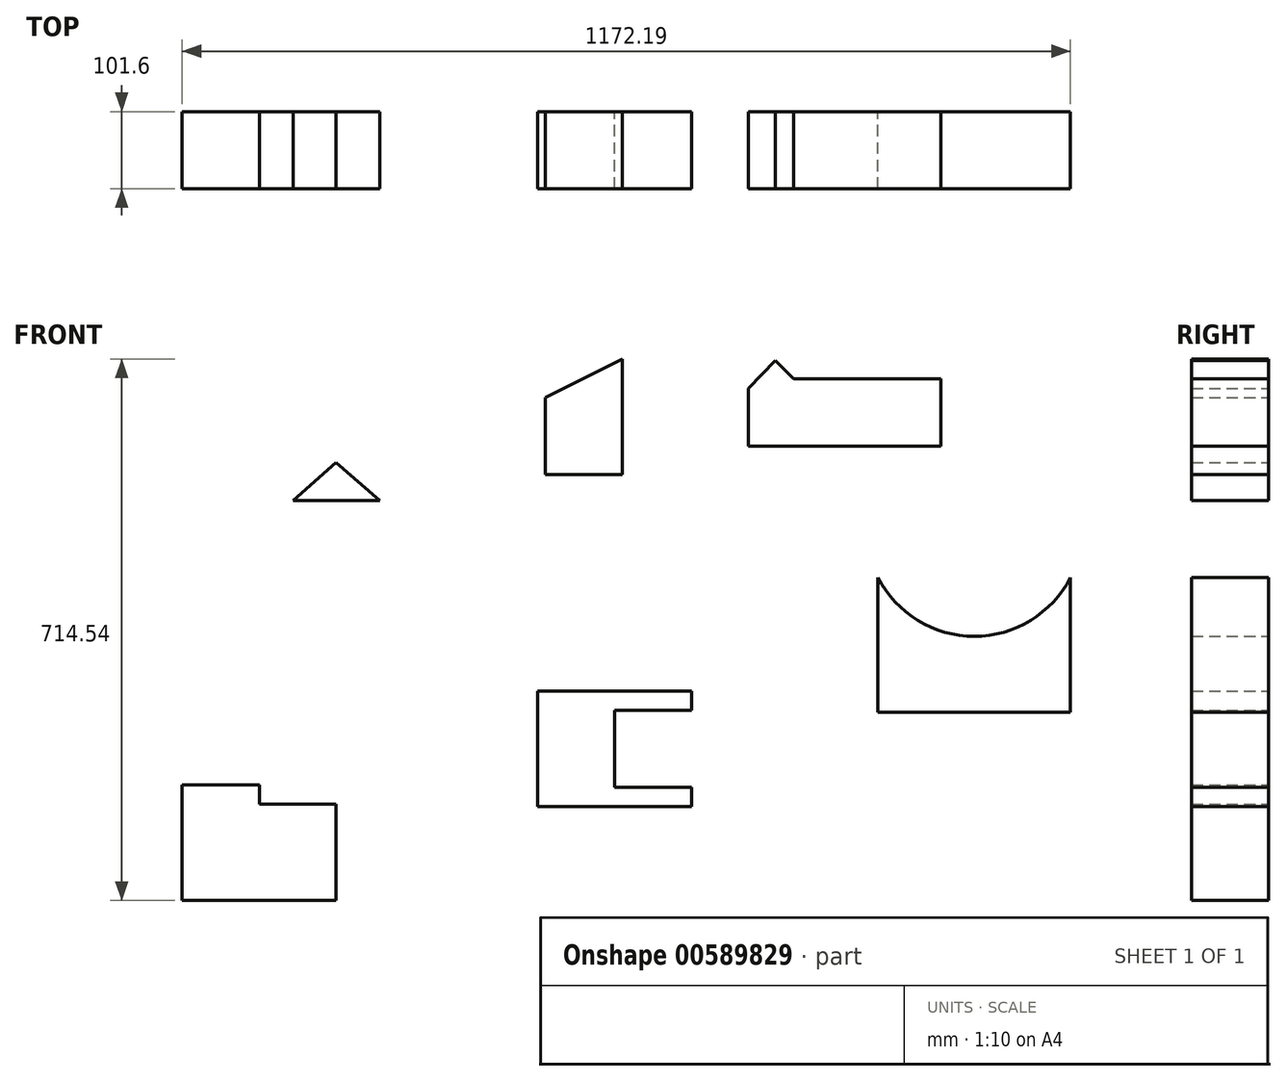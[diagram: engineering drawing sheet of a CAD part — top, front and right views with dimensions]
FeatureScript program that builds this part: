
annotation { "Feature Type Name" : "Feature", "Feature Type Description" : "" }
export const myFeature = defineFeature(function(context is Context, id is Id, definition is map)
    precondition{}
    {
        {
            var Q0;
            Q0=qCreatedBy(makeId("Front.planeOp"),FACE);
            var sketch = newSketch(context, id + "F0", { "sketchPlane" : qUnion([Q0])});
            skLineSegment(sketch, "E0", {"start": v(0, 0) * mm, "end": v(-114.3, -100.8) * mm});
            skLineSegment(sketch, "E1", {"start": v(-114.3, -100.8) * mm, "end": v(114.3, -100.8) * mm});
            skLineSegment(sketch, "E2", {"start": v(0, 0) * mm, "end": v(114.3, -100.8) * mm});
            skLineSegment(sketch, "E3", {"start": v(-57.15, -50.4) * mm, "end": v(57.15, -50.4) * mm});
            skSolve(sketch);
        }
        {
            var Q0;
            {var subQ0=sQuery(id+"F0.wireOp",EDGE,"E1");Q0=makeQuery(id+"F0.imprint","IMPRINT",FACE,{"disambiguationData":[TD([[makeQuery(id+"F0.imprint","IMPRINT",EDGE,{"derivedFrom":subQ0}),1.0]])]});}
            var sketch = newSketch(context, id + "F1", { "sketchPlane" : qUnion([Q0])});
            skSolve(sketch);
        }
        {
            var Q0;
            {var subQ3=sQuery(id+"F0.wireOp",EDGE,"E3");Q0=makeQuery(id+"F0.imprint","IMPRINT",FACE,{"disambiguationData":[TD([[makeQuery(id+"F0.imprint","IMPRINT",EDGE,{"derivedFrom":subQ3}),1.0]])]});}
            var Q1;
            {var subQ0=sQuery(id+"F0.wireOp",EDGE,"E1");Q1=makeQuery(id+"F1.imprint","IMPRINT",FACE,{"disambiguationData":[TD([[makeQuery(id+"F1.imprint","IMPRINT",EDGE,{"derivedFrom":makeQuery(id+"F0.imprint","IMPRINT",EDGE,{"derivedFrom":subQ0})}),1.0]])]});}
            extrude(context, id + "F2", {"entities" : qUnion([Q0, Q1]), "depth" : 101.6 * mm, "offsetDistance" : 25.4 * mm});
        }
        {
            var Q0;
            Q0=qCreatedBy(makeId("Front.planeOp"),FACE);
            var sketch = newSketch(context, id + "F3", { "sketchPlane" : qUnion([Q0])});
            skLineSegment(sketch, "E4", {"start": v(377.76, 136.53) * mm, "end": v(377.76, -15.87) * mm});
            skLineSegment(sketch, "E5", {"start": v(377.76, -15.87) * mm, "end": v(276.16, -15.87) * mm});
            skLineSegment(sketch, "E6", {"start": v(276.16, -15.87) * mm, "end": v(276.16, 85.73) * mm});
            skLineSegment(sketch, "E7", {"start": v(276.16, 85.73) * mm, "end": v(377.76, 136.53) * mm});
            skLineSegment(sketch, "E8", {"start": v(543.89, 21.92) * mm, "end": v(543.89, 98.12) * mm});
            skLineSegment(sketch, "E9", {"start": v(543.89, 21.92) * mm, "end": v(645.49, 21.92) * mm});
            skLineSegment(sketch, "E10", {"start": v(645.49, 21.92) * mm, "end": v(797.89, 21.92) * mm});
            skPoint(sketch, "E10.endSnap0", {"position": v(594.69, 21.92) * mm});
            skLineSegment(sketch, "E11", {"start": v(797.89, 21.92) * mm, "end": v(797.89, 72.72) * mm});
            skLineSegment(sketch, "E12", {"start": v(797.89, 72.72) * mm, "end": v(797.89, 110.82) * mm});
            skLineSegment(sketch, "E13", {"start": v(543.89, 98.12) * mm, "end": v(579.44, 134.4) * mm});
            skLineSegment(sketch, "E14", {"start": v(797.89, 110.82) * mm, "end": v(603.52, 110.82) * mm});
            skLineSegment(sketch, "E15", {"start": v(594.69, 21.92) * mm, "end": v(594.69, 72.72) * mm});
            skLineSegment(sketch, "E16", {"start": v(594.69, 72.72) * mm, "end": v(594.69, 119.47) * mm});
            skLineSegment(sketch, "E17", {"start": v(594.69, 72.72) * mm, "end": v(797.89, 72.72) * mm});
            skLineSegment(sketch, "E18", {"start": v(579.44, 134.4) * mm, "end": v(642.41, 72.72) * mm});
            skSolve(sketch);
        }
        {
            var Q0;
            Q0=makeQuery(id+"F3.imprint","IMPRINT",FACE,{"disambiguationData":[TD([[makeQuery(id+"F3.imprint","IMPRINT",EDGE,{"derivedFrom":sQuery(id+"F3.wireOp",EDGE,"E4")}),-1.0]])]});
            var Q1;
            {var subQ3=sQuery(id+"F3.wireOp",EDGE,"E8");Q1=makeQuery(id+"F3.imprint","IMPRINT",FACE,{"disambiguationData":[TD([[makeQuery(id+"F3.imprint","IMPRINT",EDGE,{"derivedFrom":subQ3}),-1.0]])]});}
            var Q2;
            {var subQ0=sQuery(id+"F3.wireOp",EDGE,"E12");Q2=makeQuery(id+"F3.imprint","IMPRINT",FACE,{"disambiguationData":[TD([[makeQuery(id+"F3.imprint","IMPRINT",EDGE,{"derivedFrom":subQ0}),1.0]])]});}
            var Q3;
            {var subQ2=sQuery(id+"F3.wireOp",EDGE,"E10");Q3=makeQuery(id+"F3.imprint","IMPRINT",FACE,{"disambiguationData":[TD([[makeQuery(id+"F3.imprint","IMPRINT",EDGE,{"derivedFrom":subQ2}),1.0]])]});}
            var Q4;
            {var subQ0=sQuery(id+"F3.wireOp",EDGE,"E16");Q4=makeQuery(id+"F3.imprint","IMPRINT",FACE,{"disambiguationData":[TD([[makeQuery(id+"F3.imprint","IMPRINT",EDGE,{"derivedFrom":subQ0}),-1.0]])]});}
            extrude(context, id + "F4", {"entities" : qUnion([Q0, Q1, Q2, Q3, Q4]), "depth" : 101.6 * mm, "offsetDistance" : 25.4 * mm});
        }
        {
            var Q0;
            Q0=qCreatedBy(makeId("Front.planeOp"),FACE);
            var sketch = newSketch(context, id + "F5", { "sketchPlane" : qUnion([Q0])});
            skLineSegment(sketch, "E19", {"start": v(-203.2, -425.61) * mm, "end": v(-101.6, -425.61) * mm});
            skLineSegment(sketch, "E20", {"start": v(-101.6, -425.61) * mm, "end": v(-101.6, -451.01) * mm});
            skLineSegment(sketch, "E21", {"start": v(-101.6, -451.01) * mm, "end": v(0, -451.01) * mm});
            skLineSegment(sketch, "E22", {"start": v(0, -451.01) * mm, "end": v(0, -578.01) * mm});
            skLineSegment(sketch, "E23", {"start": v(0, -578.01) * mm, "end": v(-203.2, -578.01) * mm});
            skLineSegment(sketch, "E24", {"start": v(-203.2, -578.01) * mm, "end": v(-203.2, -425.61) * mm});
            skSolve(sketch);
        }
        {
            var Q0;
            Q0=makeQuery(id+"F5.imprint","IMPRINT",FACE,{"disambiguationData":[TD([[makeQuery(id+"F5.imprint","IMPRINT",EDGE,{"derivedFrom":sQuery(id+"F5.wireOp",EDGE,"E19")}),-1.0]])]});
            extrude(context, id + "F6", {"entities" : qUnion([Q0]), "depth" : 101.6 * mm, "offsetDistance" : 25.4 * mm});
        }
        {
            var Q0;
            Q0=qCreatedBy(makeId("Front.planeOp"),FACE);
            var sketch = newSketch(context, id + "F7", { "sketchPlane" : qUnion([Q0])});
            skLineSegment(sketch, "E25", {"start": v(265.58, -301.3) * mm, "end": v(265.58, -453.7) * mm});
            skLineSegment(sketch, "E26", {"start": v(265.58, -453.7) * mm, "end": v(468.78, -453.7) * mm});
            skLineSegment(sketch, "E27", {"start": v(468.78, -453.7) * mm, "end": v(468.78, -301.3) * mm});
            skLineSegment(sketch, "E28", {"start": v(468.78, -301.3) * mm, "end": v(265.58, -301.3) * mm});
            skLineSegment(sketch, "E29", {"start": v(468.78, -326.7) * mm, "end": v(367.18, -326.7) * mm});
            skLineSegment(sketch, "E30", {"start": v(468.78, -428.3) * mm, "end": v(367.18, -428.3) * mm});
            skLineSegment(sketch, "E31", {"start": v(367.18, -428.3) * mm, "end": v(367.18, -326.7) * mm});
            skSolve(sketch);
        }
        {
            var Q0;
            Q0=makeQuery(id+"F7.imprint","IMPRINT",FACE,{"disambiguationData":[TD([[makeQuery(id+"F7.imprint","IMPRINT",EDGE,{"derivedFrom":sQuery(id+"F7.wireOp",EDGE,"E25")}),1.0]])]});
            extrude(context, id + "F8", {"entities" : qUnion([Q0]), "depth" : 101.6 * mm, "offsetDistance" : 25.4 * mm});
        }
        {
            var Q0;
            Q0=qCreatedBy(makeId("Front.planeOp"),FACE);
            var sketch = newSketch(context, id + "F9", { "sketchPlane" : qUnion([Q0])});
            skLineSegment(sketch, "E32", {"start": v(715, -151.64) * mm, "end": v(715, -329.44) * mm});
            skLineSegment(sketch, "E33", {"start": v(715, -329.44) * mm, "end": v(969, -329.44) * mm});
            skLineSegment(sketch, "E34", {"start": v(969, -329.44) * mm, "end": v(969, -151.64) * mm});
            skLineSegment(sketch, "E35", {"start": v(715, -151.64) * mm, "end": v(969, -151.64) * mm});
            skArc(sketch, "E36", {"start": v(715, -151.64) * mm, "mid": v(842, -229.23) * mm, "end": v(969, -151.64) * mm});
            skSolve(sketch);
        }
        {
            var Q0;
            Q0=makeQuery(id+"F9.imprint","IMPRINT",FACE,{"disambiguationData":[TD([[makeQuery(id+"F9.imprint","IMPRINT",EDGE,{"derivedFrom":sQuery(id+"F9.wireOp",EDGE,"E32")}),1.0]])]});
            extrude(context, id + "F10", {"entities" : qUnion([Q0]), "depth" : 101.6 * mm, "offsetDistance" : 25.4 * mm});
        }
    });
